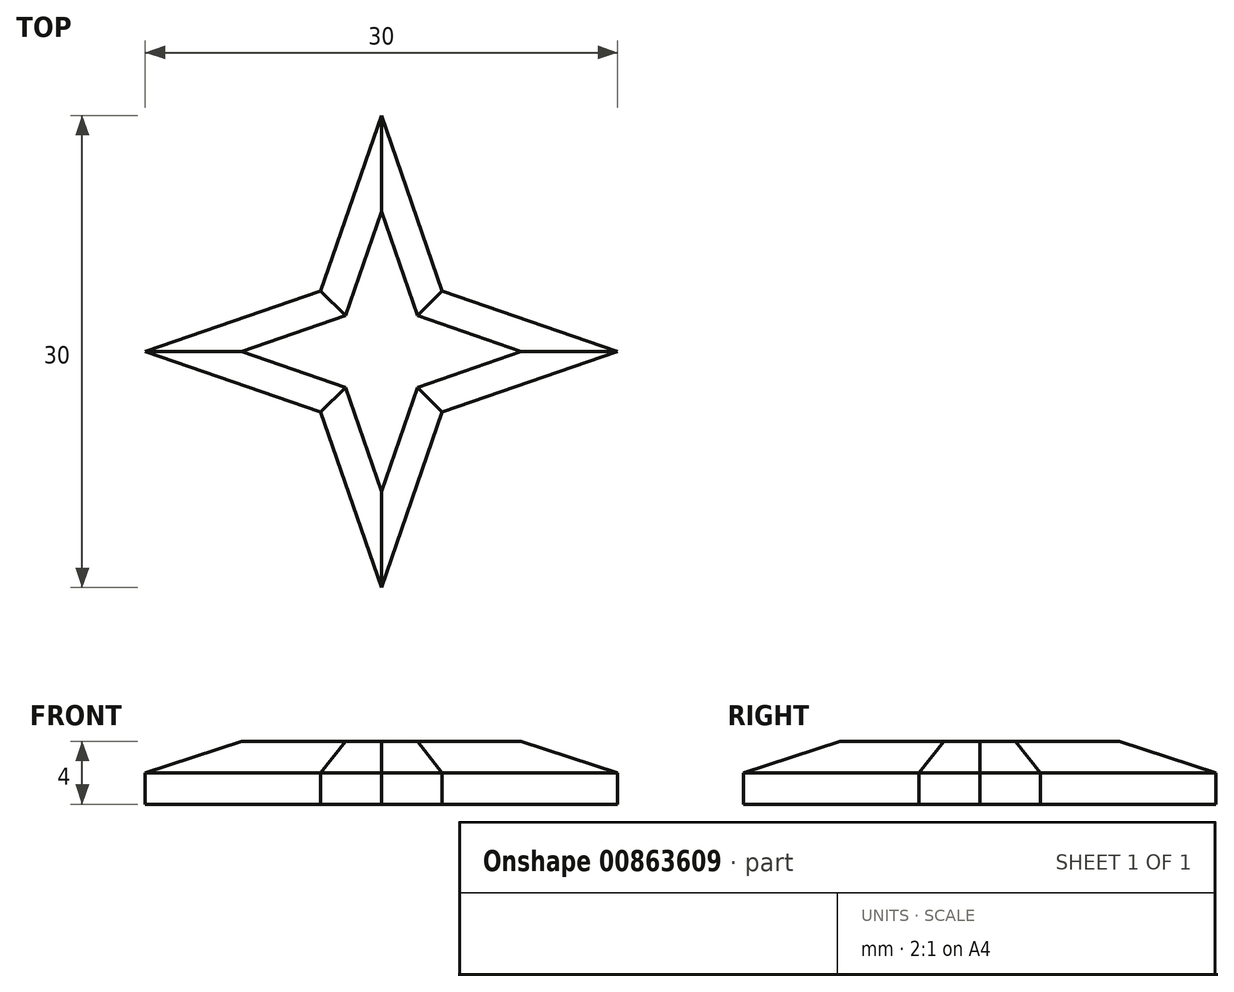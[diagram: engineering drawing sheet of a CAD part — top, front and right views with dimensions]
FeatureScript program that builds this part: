
annotation { "Feature Type Name" : "Feature", "Feature Type Description" : "" }
export const myFeature = defineFeature(function(context is Context, id is Id, definition is map)
    precondition{}
    {
        {
            var Q0;
            Q0=qCreatedBy(makeId("Top.planeOp"),FACE);
            var sketch = newSketch(context, id + "F0", { "sketchPlane" : qUnion([Q0])});
            skLineSegment(sketch, "E0", {"start": v(0, 15) * mm, "end": v(-3.85, 3.85) * mm});
            skLineSegment(sketch, "E1", {"start": v(0, 15) * mm, "end": v(3.85, 3.85) * mm});
            skLineSegment(sketch, "E2", {"start": v(3.85, 3.85) * mm, "end": v(0, 0) * mm});
            skLineSegment(sketch, "E3", {"start": v(0, 0) * mm, "end": v(-3.85, 3.85) * mm});
            skLineSegment(sketch, "E4.1.0", {"start": v(-15, 0) * mm, "end": v(-3.85, -3.85) * mm});
            skLineSegment(sketch, "E4.1.1", {"start": v(0, 0) * mm, "end": v(-3.85, -3.85) * mm});
            skLineSegment(sketch, "E4.1.2", {"start": v(-15, 0) * mm, "end": v(-3.85, 3.85) * mm});
            skLineSegment(sketch, "E4.1.3", {"start": v(-3.85, 3.85) * mm, "end": v(0, 0) * mm});
            skLineSegment(sketch, "E4.2.0", {"start": v(0, -15) * mm, "end": v(3.85, -3.85) * mm});
            skLineSegment(sketch, "E4.2.1", {"start": v(0, 0) * mm, "end": v(3.85, -3.85) * mm});
            skLineSegment(sketch, "E4.2.2", {"start": v(0, -15) * mm, "end": v(-3.85, -3.85) * mm});
            skLineSegment(sketch, "E4.2.3", {"start": v(-3.85, -3.85) * mm, "end": v(0, 0) * mm});
            skLineSegment(sketch, "E4.3.0", {"start": v(15, 0) * mm, "end": v(3.85, 3.85) * mm});
            skLineSegment(sketch, "E4.3.1", {"start": v(0, 0) * mm, "end": v(3.85, 3.85) * mm});
            skLineSegment(sketch, "E4.3.2", {"start": v(15, 0) * mm, "end": v(3.85, -3.85) * mm});
            skLineSegment(sketch, "E4.3.3", {"start": v(3.85, -3.85) * mm, "end": v(0, 0) * mm});
            skPoint(sketch, "E4.center", {"position": v(0, 0) * mm});
            skSolve(sketch);
        }
        {
            var Q0;
            Q0=makeQuery(id+"F0.imprint","IMPRINT",FACE,{"disambiguationData":[TD([[makeQuery(id+"F0.imprint","IMPRINT",EDGE,{"derivedFrom":sQuery(id+"F0.wireOp",EDGE,"E4.1.0")}),1.0]])]});
            var Q1;
            Q1=makeQuery(id+"F0.imprint","IMPRINT",FACE,{"disambiguationData":[TD([[makeQuery(id+"F0.imprint","IMPRINT",EDGE,{"derivedFrom":sQuery(id+"F0.wireOp",EDGE,"E0")}),1.0]])]});
            var Q2;
            Q2=makeQuery(id+"F0.imprint","IMPRINT",FACE,{"disambiguationData":[TD([[makeQuery(id+"F0.imprint","IMPRINT",EDGE,{"derivedFrom":sQuery(id+"F0.wireOp",EDGE,"E4.3.0")}),1.0]])]});
            var Q3;
            Q3=makeQuery(id+"F0.imprint","IMPRINT",FACE,{"disambiguationData":[TD([[makeQuery(id+"F0.imprint","IMPRINT",EDGE,{"derivedFrom":sQuery(id+"F0.wireOp",EDGE,"E4.2.0")}),1.0]])]});
            extrude(context, id + "F1", {"entities" : qUnion([Q0, Q1, Q2, Q3]), "depth" : 4 * mm, "offsetDistance" : 25 * mm});
        }
        {
            var Q0;
            Q0=makeQuery(id+"F1.opExtrude","CAP_EDGE",EDGE,{"disambiguationData":[OSD([sQuery(id+"F0.wireOp",EDGE,"E4.1.0")])],"isStart":false});
            var Q1;
            Q1=makeQuery(id+"F1.opExtrude","CAP_EDGE",EDGE,{"disambiguationData":[OSD([sQuery(id+"F0.wireOp",EDGE,"E4.2.2")])],"isStart":false});
            var Q2;
            Q2=makeQuery(id+"F1.opExtrude","CAP_EDGE",EDGE,{"disambiguationData":[OSD([sQuery(id+"F0.wireOp",EDGE,"E4.2.0")])],"isStart":false});
            var Q3;
            Q3=makeQuery(id+"F1.opExtrude","CAP_EDGE",EDGE,{"disambiguationData":[OSD([sQuery(id+"F0.wireOp",EDGE,"E4.3.2")])],"isStart":false});
            var Q4;
            Q4=makeQuery(id+"F1.opExtrude","CAP_EDGE",EDGE,{"disambiguationData":[OSD([sQuery(id+"F0.wireOp",EDGE,"E4.3.0")])],"isStart":false});
            var Q5;
            Q5=makeQuery(id+"F1.opExtrude","CAP_EDGE",EDGE,{"disambiguationData":[OSD([sQuery(id+"F0.wireOp",EDGE,"E1")])],"isStart":false});
            var Q6;
            Q6=makeQuery(id+"F1.opExtrude","CAP_EDGE",EDGE,{"disambiguationData":[OSD([sQuery(id+"F0.wireOp",EDGE,"E0")])],"isStart":false});
            var Q7;
            Q7=makeQuery(id+"F1.opExtrude","CAP_EDGE",EDGE,{"disambiguationData":[OSD([sQuery(id+"F0.wireOp",EDGE,"E4.1.2")])],"isStart":false});
            chamfer(context, id + "F2", {"entities" : qUnion([Q0, Q1, Q2, Q3, Q4, Q5, Q6, Q7]), "width" : 2 * mm, "tangentPropagation" : true});
        }
    });
